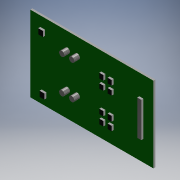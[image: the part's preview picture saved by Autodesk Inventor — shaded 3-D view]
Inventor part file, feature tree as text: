
AUTODESK INVENTOR PART (.ipt)
format: ipt  version: 2019.4 (Build 234330000, 330)  size: 168,960 bytes
history: native  units: mm
features: extrude x3, sketch x3
ambient origin geometry x8: Origin, YZ Plane, XZ Plane, XY Plane, X Axis, Y Axis, Z Axis, Center Point
bodies: Solid1 (feature_tree)
feature tree (6):
  extrude  "Extrusion1"  Depth=2.5mm TaperAngle=0.0deg
  extrude  "Extrusion2"  [1 undecoded]
  extrude  "Extrusion3"  [1 undecoded]
  sketch  "Sketch1"  dims[d0=2.5mm d1=0.0mm d2=2.5mm d3=0.0mm]
  sketch  "Sketch2"  dims[d4=6.75mm d5=0.0mm]
  sketch  "Sketch3"
note: 2 required parameter values undecoded (feature->parameter linkage not recoverable at this tier; creation-order binding heuristic only, values carry confidence <= 0.55)
